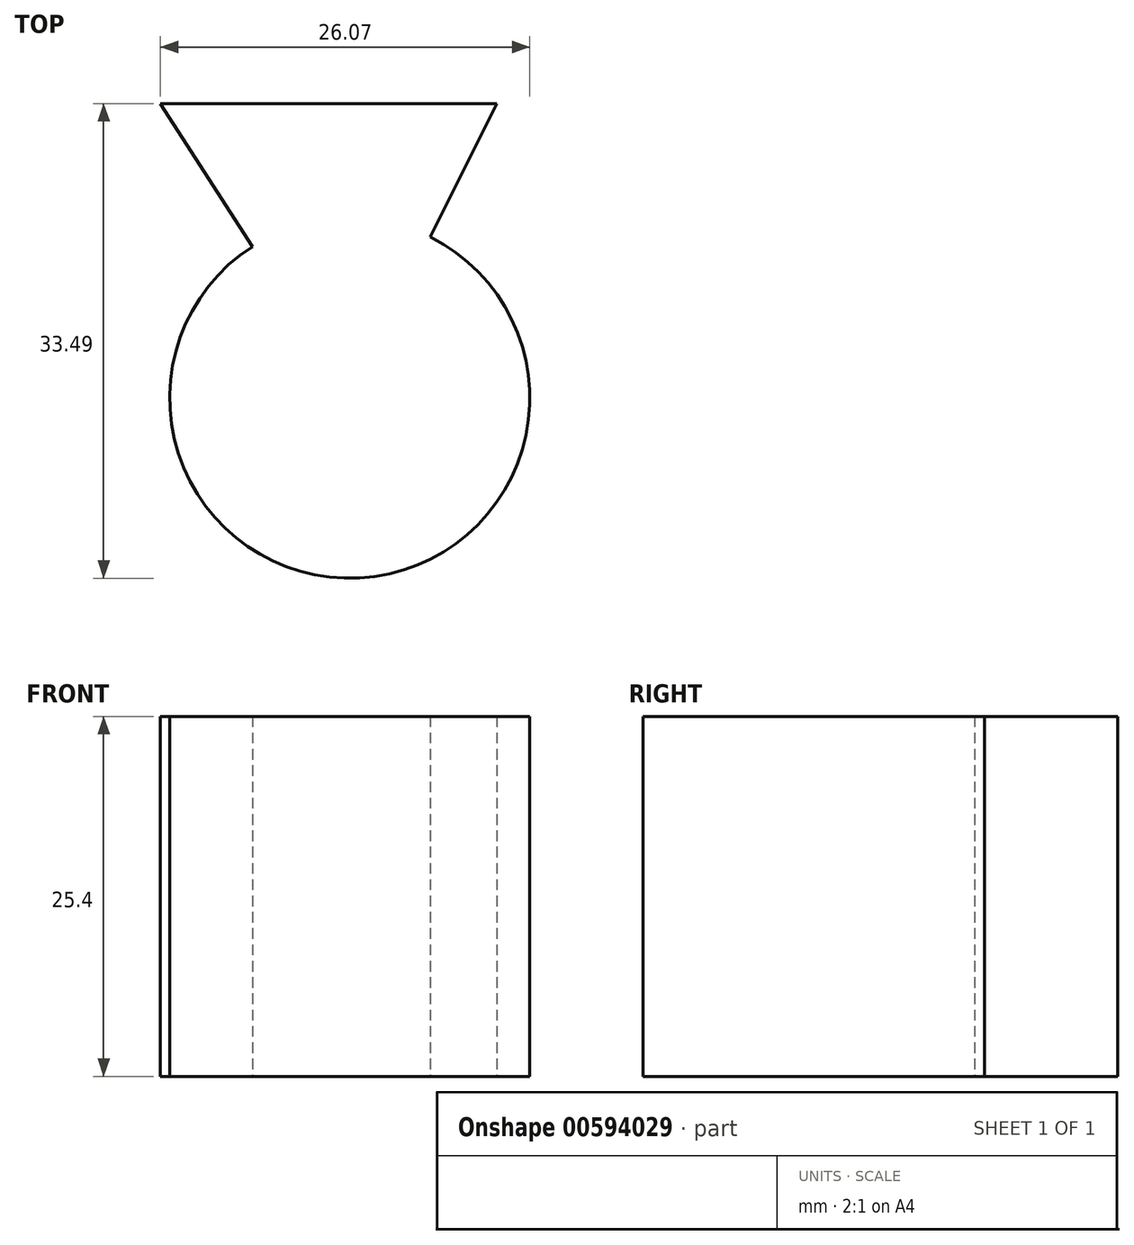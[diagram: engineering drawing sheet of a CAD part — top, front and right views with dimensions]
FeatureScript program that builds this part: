
annotation { "Feature Type Name" : "Feature", "Feature Type Description" : "" }
export const myFeature = defineFeature(function(context is Context, id is Id, definition is map)
    precondition{}
    {
        {
            var Q0;
            Q0=qCreatedBy(makeId("Top.planeOp"),FACE);
            var sketch = newSketch(context, id + "F0", { "sketchPlane" : qUnion([Q0])});
            skCircle(sketch, "E0", {"center": v(0, 0) * mm, "radius": 12.7 * mm});
            skLineSegment(sketch, "E1", {"start": v(0, 0) * mm, "end": v(-13.36, 20.78) * mm});
            skLineSegment(sketch, "E2", {"start": v(-13.36, 20.78) * mm, "end": v(10.39, 20.78) * mm});
            skLineSegment(sketch, "E3", {"start": v(10.39, 20.78) * mm, "end": v(0, 0) * mm});
            skSolve(sketch);
        }
        {
            var Q0;
            {var subQ0=sQuery(id+"F0.wireOp",EDGE,"E1");var subQ1=sQuery(id+"F0.wireOp",EDGE,"E0");var subQ2=makeQuery(id+"F0.imprint","INTERSECT",VERTEX,{"derivedFrom":[subQ1,subQ0]});Q0=makeQuery(id+"F0.imprint","IMPRINT",FACE,{"disambiguationData":[TD([[makeQuery(id+"F0.imprint","IMPRINT",EDGE,{"disambiguationData":[TD([[subQ2,-1.0]])],"derivedFrom":subQ1}),1.0]])]});}
            var Q1;
            {var subQ0=sQuery(id+"F0.wireOp",EDGE,"E1");var subQ1=sQuery(id+"F0.wireOp",EDGE,"E0");var subQ2=makeQuery(id+"F0.imprint","INTERSECT",VERTEX,{"derivedFrom":[subQ1,subQ0]});Q1=makeQuery(id+"F0.imprint","IMPRINT",FACE,{"disambiguationData":[TD([[makeQuery(id+"F0.imprint","IMPRINT",EDGE,{"disambiguationData":[TD([[subQ2,1.0]])],"derivedFrom":subQ1}),1.0]])]});}
            extrude(context, id + "F1", {"entities" : qUnion([Q0, Q1]), "depth" : 20.32 * mm, "offsetDistance" : 25.4 * mm});
        }
        {
            var Q0;
            Q0 = qSketchRegion(id + "F0", true);
            extrude(context, id + "F2", {"entities" : qUnion([Q0]), "operationType" : NewBodyOperationType.ADD, "depth" : 25.4 * mm, "offsetDistance" : 25.4 * mm});
        }
    });
